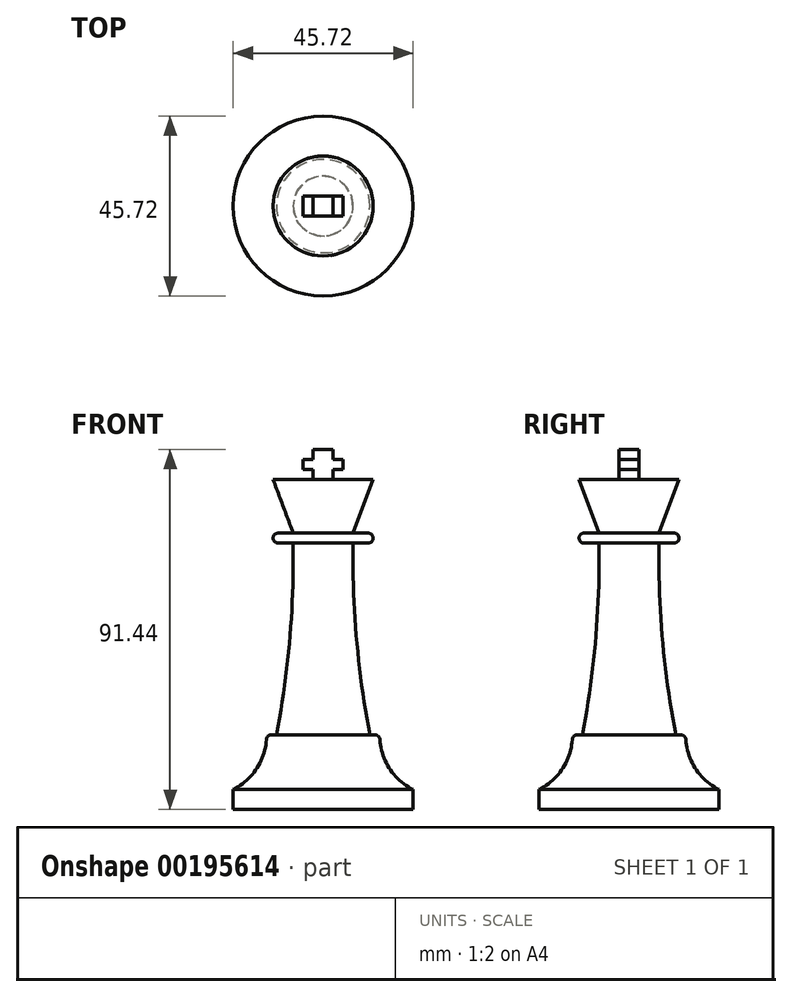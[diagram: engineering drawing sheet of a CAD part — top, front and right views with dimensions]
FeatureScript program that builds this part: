
annotation { "Feature Type Name" : "Feature", "Feature Type Description" : "" }
export const myFeature = defineFeature(function(context is Context, id is Id, definition is map)
    precondition{}
    {
        {
            var Q0;
            Q0=qCreatedBy(makeId("Front.planeOp"),FACE);
            var sketch = newSketch(context, id + "F0", { "sketchPlane" : qUnion([Q0])});
            skLineSegment(sketch, "E0", {"start": v(0, 0) * mm, "end": v(0, 83.82) * mm});
            skLineSegment(sketch, "E1", {"start": v(0, 0) * mm, "end": v(22.86, 0) * mm});
            skLineSegment(sketch, "E2", {"start": v(22.86, 0) * mm, "end": v(22.86, 5.08) * mm});
            skArc(sketch, "E3", {"start": v(14.4, 18.95) * mm, "mid": v(16.62, 10.8) * mm, "end": v(22.86, 5.08) * mm});
            skLineSegment(sketch, "E4", {"start": v(14.4, 18.95) * mm, "end": v(11.85, 18.95) * mm});
            skLineSegment(sketch, "E5", {"start": v(0, 83.82) * mm, "end": v(12.7, 83.82) * mm});
            skLineSegment(sketch, "E6", {"start": v(12.7, 83.82) * mm, "end": v(7.62, 70.21) * mm});
            skLineSegment(sketch, "E7", {"start": v(7.62, 70.21) * mm, "end": v(11.43, 70.21) * mm});
            skLineSegment(sketch, "E8", {"start": v(11.43, 67.67) * mm, "end": v(7.62, 67.67) * mm});
            skArc(sketch, "E9", {"start": v(7.62, 67.67) * mm, "mid": v(8.5, 43.2) * mm, "end": v(11.85, 18.95) * mm});
            skArc(sketch, "E10", {"start": v(11.43, 67.67) * mm, "mid": v(12.7, 68.94) * mm, "end": v(11.43, 70.21) * mm});
            skSolve(sketch);
        }
        {
            var Q0;
            Q0=makeQuery(id+"F0.imprint","IMPRINT",FACE,{"disambiguationData":[TD([[makeQuery(id+"F0.imprint","IMPRINT",EDGE,{"derivedFrom":sQuery(id+"F0.wireOp",EDGE,"E0")}),-1.0]])]});
            var Q1;
            Q1=sQuery(id+"F0.wireOp",EDGE,"E0");
            revolve(context, id + "F1", {"entities" : qUnion([Q0]), "axis" : qUnion([Q1]), "revolveType" : RevolveType.FULL});
        }
        {
            var Q0;
            Q0=makeQuery(id+"F1.opRevolve","SWEPT_FACE",FACE,{"disambiguationData":[OSD([sQuery(id+"F0.wireOp",EDGE,"E5")])]});
            var sketch = newSketch(context, id + "F2", { "sketchPlane" : qUnion([Q0])});
            skLineSegment(sketch, "E11.bottom", {"start": v(-2.54, 2.54) * mm, "end": v(2.54, 2.54) * mm});
            skLineSegment(sketch, "E11.top", {"start": v(-2.54, -2.54) * mm, "end": v(2.54, -2.54) * mm});
            skLineSegment(sketch, "E11.left", {"start": v(-2.54, 2.54) * mm, "end": v(-2.54, -2.54) * mm});
            skLineSegment(sketch, "E11.right", {"start": v(2.54, 2.54) * mm, "end": v(2.54, -2.54) * mm});
            skSolve(sketch);
        }
        {
            var Q0;
            Q0=makeQuery(id+"F2.imprint","IMPRINT",FACE,{"disambiguationData":[TD([[makeQuery(id+"F2.imprint","IMPRINT",EDGE,{"derivedFrom":sQuery(id+"F2.wireOp",EDGE,"E11.bottom")}),-1.0]])]});
            extrude(context, id + "F3", {"entities" : qUnion([Q0]), "operationType" : NewBodyOperationType.ADD, "depth" : 2.54 * mm});
        }
        {
            var Q0;
            Q0=makeQuery(id+"F3.opExtrude","CAP_FACE",FACE,{"disambiguationData":[OSD([sQuery(id+"F2.wireOp",EDGE,"E11.bottom"),sQuery(id+"F2.wireOp",EDGE,"E11.top"),sQuery(id+"F2.wireOp",EDGE,"E11.left"),sQuery(id+"F2.wireOp",EDGE,"E11.right")])],"isStart":false});
            var sketch = newSketch(context, id + "F4", { "sketchPlane" : qUnion([Q0])});
            skLineSegment(sketch, "E12.bottom", {"start": v(-5.08, 2.54) * mm, "end": v(5.08, 2.54) * mm});
            skLineSegment(sketch, "E12.top", {"start": v(-5.08, -2.54) * mm, "end": v(5.08, -2.54) * mm});
            skLineSegment(sketch, "E12.left", {"start": v(-5.08, 2.54) * mm, "end": v(-5.08, -2.54) * mm});
            skLineSegment(sketch, "E12.right", {"start": v(5.08, 2.54) * mm, "end": v(5.08, -2.54) * mm});
            skSolve(sketch);
        }
        {
            var Q0;
            {var subQ2=sQuery(id+"F4.wireOp",EDGE,"E12.left");Q0=makeQuery(id+"F4.imprint","IMPRINT",FACE,{"disambiguationData":[TD([[makeQuery(id+"F4.imprint","IMPRINT",EDGE,{"derivedFrom":subQ2}),1.0]])]});}
            var Q1;
            {var subQ1=makeQuery(id+"F3.opExtrude","CAP_EDGE",EDGE,{"disambiguationData":[OSD([sQuery(id+"F2.wireOp",EDGE,"E11.left")])],"isStart":false});Q1=makeQuery(id+"F4.imprint","IMPRINT",FACE,{"disambiguationData":[TD([[makeQuery(id+"F4.imprint","IMPRINT",EDGE,{"derivedFrom":subQ1}),1.0]])]});}
            var Q2;
            {var subQ2=sQuery(id+"F4.wireOp",EDGE,"E12.right");Q2=makeQuery(id+"F4.imprint","IMPRINT",FACE,{"disambiguationData":[TD([[makeQuery(id+"F4.imprint","IMPRINT",EDGE,{"derivedFrom":subQ2}),-1.0]])]});}
            extrude(context, id + "F5", {"entities" : qUnion([Q0, Q1, Q2]), "operationType" : NewBodyOperationType.ADD, "depth" : 2.54 * mm});
        }
        {
            var Q0;
            Q0=makeQuery(id+"F5.opExtrude","CAP_FACE",FACE,{"disambiguationData":[OSD([sQuery(id+"F4.wireOp",EDGE,"E12.bottom"),sQuery(id+"F4.wireOp",EDGE,"E12.top"),sQuery(id+"F4.wireOp",EDGE,"E12.left"),sQuery(id+"F4.wireOp",EDGE,"E12.right")])],"isStart":false});
            var sketch = newSketch(context, id + "F6", { "sketchPlane" : qUnion([Q0])});
            skLineSegment(sketch, "E13.bottom", {"start": v(-2.54, 2.54) * mm, "end": v(2.54, 2.54) * mm});
            skLineSegment(sketch, "E13.top", {"start": v(-2.54, -2.54) * mm, "end": v(2.54, -2.54) * mm});
            skLineSegment(sketch, "E13.left", {"start": v(-2.54, 2.54) * mm, "end": v(-2.54, -2.54) * mm});
            skLineSegment(sketch, "E13.right", {"start": v(2.54, 2.54) * mm, "end": v(2.54, -2.54) * mm});
            skSolve(sketch);
        }
        {
            var Q0;
            Q0=makeQuery(id+"F6.imprint","IMPRINT",FACE,{"disambiguationData":[TD([[makeQuery(id+"F6.imprint","IMPRINT",EDGE,{"derivedFrom":sQuery(id+"F6.wireOp",EDGE,"E13.bottom")}),-1.0]])]});
            extrude(context, id + "F7", {"entities" : qUnion([Q0]), "operationType" : NewBodyOperationType.ADD, "depth" : 2.54 * mm});
        }
        {
            var Q0;
            Q0=makeQuery(id+"F1.opRevolve","SWEPT_EDGE",EDGE,{"disambiguationData":[OSD([sQuery(id+"F0.wireOp",EDGE,"E3"),sQuery(id+"F0.wireOp",EDGE,"E4")])]});
            fillet(context, id + "F8", {"entities" : qUnion([Q0]), "radius" : 1.27 * mm, "tangentPropagation" : true, "allowEdgeOverflow" : false});
        }
    });
